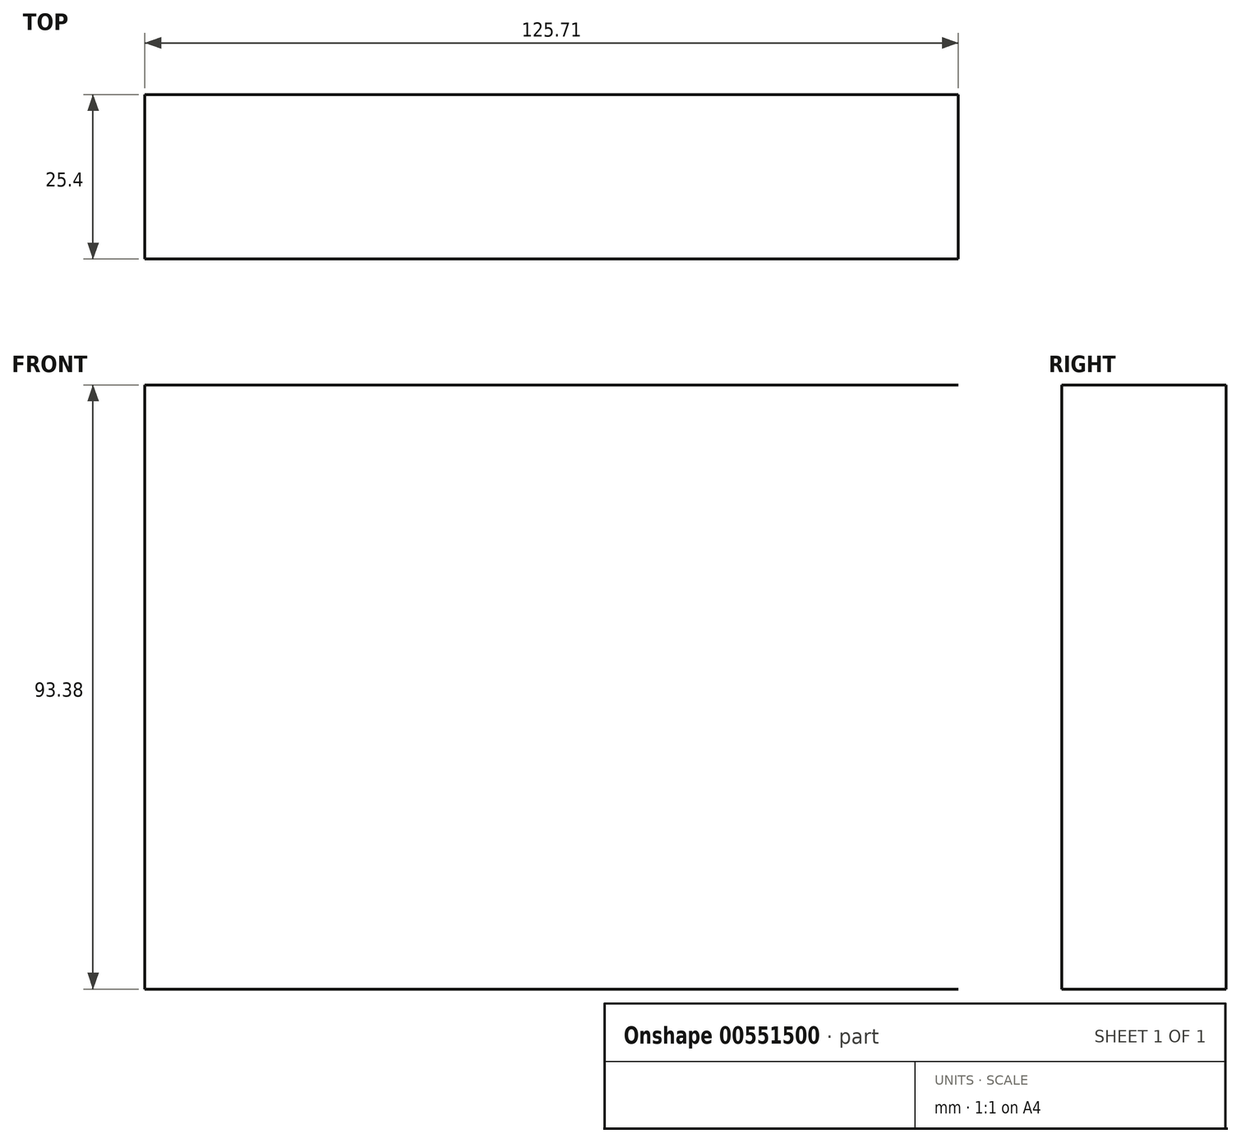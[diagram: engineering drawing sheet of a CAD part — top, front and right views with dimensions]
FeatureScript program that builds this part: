
annotation { "Feature Type Name" : "Feature", "Feature Type Description" : "" }
export const myFeature = defineFeature(function(context is Context, id is Id, definition is map)
    precondition{}
    {
        {
            var Q0;
            Q0=qCreatedBy(makeId("Front.planeOp"),FACE);
            var sketch = newSketch(context, id + "F0", { "sketchPlane" : qUnion([Q0])});
            skLineSegment(sketch, "E0.bottom", {"start": v(-42.1, 59.8) * mm, "end": v(83.61, 59.8) * mm});
            skLineSegment(sketch, "E0.top", {"start": v(-42.1, -33.58) * mm, "end": v(83.61, -33.58) * mm});
            skLineSegment(sketch, "E0.left", {"start": v(-42.1, 59.8) * mm, "end": v(-42.1, -33.58) * mm});
            skLineSegment(sketch, "E0.right", {"start": v(83.61, 59.8) * mm, "end": v(83.61, -33.58) * mm});
            skSolve(sketch);
        }
        {
            var Q0;
            Q0=sQuery(id+"F0.wireOp",EDGE,"E0.bottom");
            var Q1;
            Q1=sQuery(id+"F0.wireOp",EDGE,"E0.left");
            var Q2;
            Q2=sQuery(id+"F0.wireOp",EDGE,"E0.top");
            extrude(context, id + "F1", {"bodyType" : ToolBodyType.SURFACE, "surfaceEntities" : qUnion([Q0, Q1, Q2]), "depth" : 25.4 * mm, "offsetDistance" : 25.4 * mm});
        }
    });
